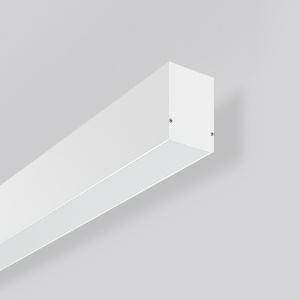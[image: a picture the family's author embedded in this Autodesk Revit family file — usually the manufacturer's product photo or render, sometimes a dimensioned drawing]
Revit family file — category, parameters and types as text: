
# Revit family: less_is_more_50_312607_002_76_a93d
name_source: partatom
category: Lighting Fixtures
units: mm (PartAtom-declared; Revit-internal decimal feet)

## family parameters
Cut with Voids When Loaded = No
Host = Face
Light Source = No
Part Type = Normal
Room Calculation Point = No
Round Connector Dimension = Use Diameter
Shared = No

## types (1)
- LESS IS MORE 50 (1 x LED Modul 830, 1450 lm, 3000)
    Apparent Load = 13 VA
    CIE Flux Codes = 48 80 96 100 100
    Color Rendering = 80
    Color Temperature = 3000
    Default Elevation = 1800 mm
    Description = Series: LESS IS MORE 50
Linear wall luminaires. Housing: extruded aluminium profile, powder-coated. End cap aluminium powder-coated. Diffuser made of non-yellowing plastic (PMMA), opal. Direct light emission. Suitable for Wall (surface). LED unit with integrated converter interchangeable and removable. Suitable for through-wiring. With sensors or as a safety luminaire on request. 
Colour: traffic white, matt (RAL 9016)
Length: 1127 mm
Width: 67 mm
Height: 75 mm
Lamp: LED
Socket: without socket
Colour temperature: 3000K
Colour rendering index (CRI): 80
System power: 13 W
Rated luminous flux: 1450 lm
Luminous efficiency: 112 lm/W
Control gear: Converter, dimmable, DALI
Protection class: I
Type of protection: IP 20
    Height = 75 mm
    Lamp = 1 x LED Modul 830
    Lamp Light Flux = 1450 lm
    Lamp count = 1
    Length = 1127 mm
    Lifetime = 50000 h
    Luminous efficacy = 112 lm/W
    Manufacturer = RZB
    ModVariant = No
    Model = 312607.002.76
    Mounting Place = Wall
    Mounting Type = Surface mounted
    Number of Poles = 1
    OnlyDefault = Yes
    Power Factor = 1
    Product Name = LESS IS MORE 50
    Product group = Surface mounted LED linear luminaires
    ProductGroupID = 2007
    Protection Class = Protection class I
    Protection Degree = IP 20
    RLX_Detail_Level = 1
    RLX_Emergency_Light_Flux = 0 lm
    RLX_Emergency_Type = 0
    RLX_Emergency_Type_DB = No
    RlxData = <blob elided: 35153 chars, md5=86aa39cd>
    Socket = socket
    Standby Power = 0 W
    System Light Flux = 1450 lm
    System Power = 13 W
    Type Comments = Product without accessories
    Type Image = 312606.002.jpg
    URL = http://relux.com
    VarID = ---
    Voltage = 0 V
    Weight = 0.00 kg
    Width = 67 mm

## geometry (parser evidence)
native form markers: Blend x4, Sweep x9
no freeform markers — native parametric forms only
